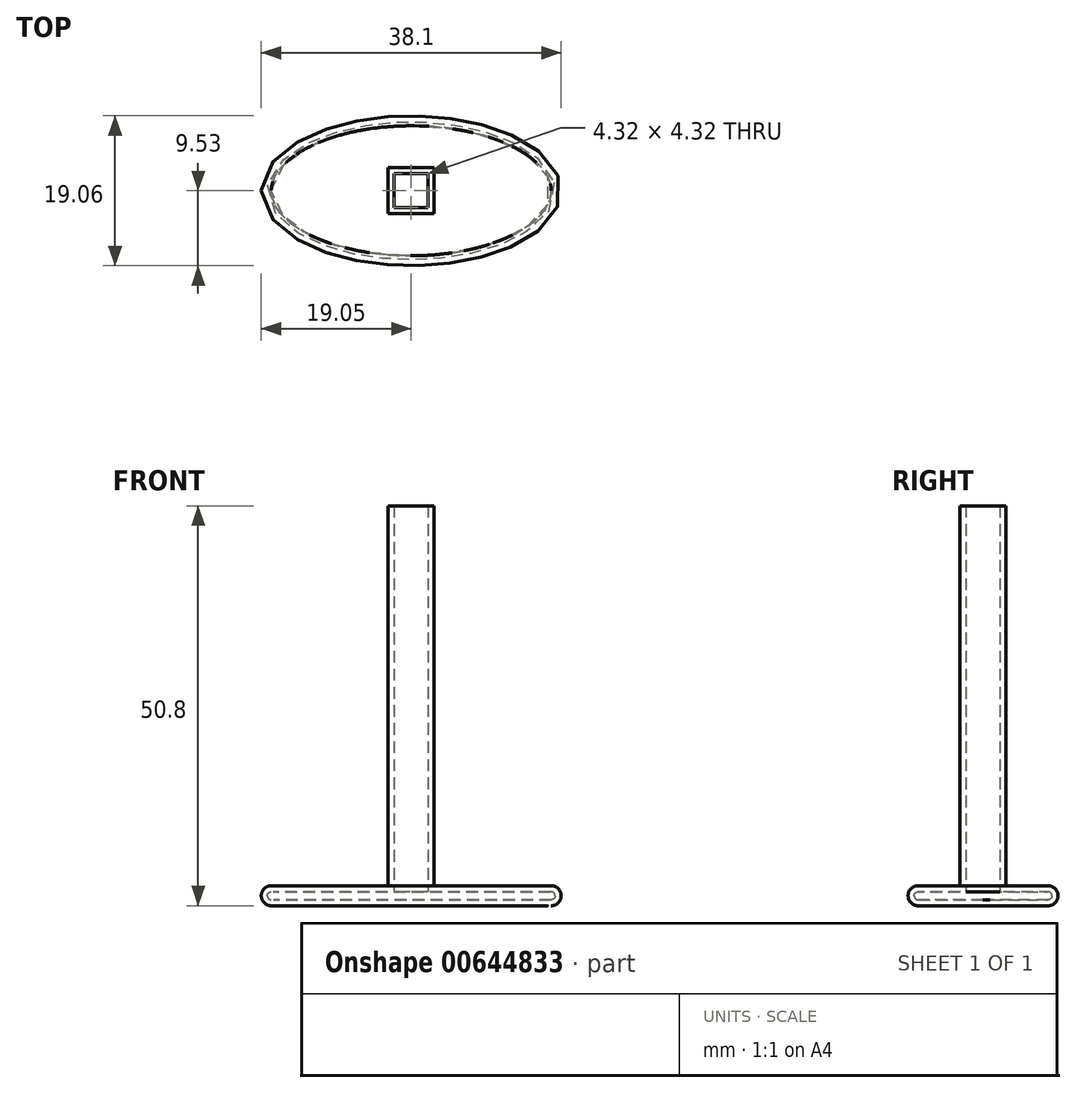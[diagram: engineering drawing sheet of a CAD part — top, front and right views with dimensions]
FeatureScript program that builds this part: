
annotation { "Feature Type Name" : "Feature", "Feature Type Description" : "" }
export const myFeature = defineFeature(function(context is Context, id is Id, definition is map)
    precondition{}
    {
        {
            var Q0;
            Q0=qCreatedBy(makeId("Top.planeOp"),FACE);
            var sketch = newSketch(context, id + "F0", { "sketchPlane" : qUnion([Q0])});
            skLineSegment(sketch, "E0.bottom", {"start": v(2.92, 2.92) * mm, "end": v(-2.92, 2.92) * mm});
            skLineSegment(sketch, "E0.top", {"start": v(2.92, -2.92) * mm, "end": v(-2.92, -2.92) * mm});
            skLineSegment(sketch, "E0.left", {"start": v(2.92, 2.92) * mm, "end": v(2.92, -2.92) * mm});
            skLineSegment(sketch, "E0.right", {"start": v(-2.92, 2.92) * mm, "end": v(-2.92, -2.92) * mm});
            skPoint(sketch, "E0.middle", {"position": v(0, 0) * mm});
            skEllipse(sketch, "E1", {"center": v(0, 0) * mm, "majorRadius": 19.05 * mm, "minorRadius": 9.53 * mm, "majorAxis": v(-1, 0)});
            skSolve(sketch);
        }
        {
            var Q0;
            Q0=makeQuery(id+"F0.imprint","IMPRINT",FACE,{"disambiguationData":[TD([[makeQuery(id+"F0.imprint","IMPRINT",EDGE,{"derivedFrom":sQuery(id+"F0.wireOp",EDGE,"E0.bottom")}),1.0]])]});
            extrude(context, id + "F1", {"entities" : qUnion([Q0]), "depth" : 50.8 * mm, "offsetDistance" : 25.4 * mm});
        }
        {
            var Q0;
            Q0=makeQuery(id+"F0.imprint","IMPRINT",FACE,{"disambiguationData":[TD([[makeQuery(id+"F0.imprint","IMPRINT",EDGE,{"derivedFrom":sQuery(id+"F0.wireOp",EDGE,"E0.bottom")}),-1.0]])]});
            extrude(context, id + "F2", {"entities" : qUnion([Q0]), "operationType" : NewBodyOperationType.ADD, "depth" : 2.54 * mm, "offsetDistance" : 25.4 * mm});
        }
        {
            var Q0;
            Q0=makeQuery(id+"F2.opExtrude","CAP_EDGE",EDGE,{"disambiguationData":[OSD([sQuery(id+"F0.wireOp",EDGE,"E1")])],"isStart":false});
            var Q1;
            Q1=makeQuery(id+"F2.opExtrude","CAP_EDGE",EDGE,{"disambiguationData":[OSD([sQuery(id+"F0.wireOp",EDGE,"E1")])],"isStart":true});
            fillet(context, id + "F3", {"entities" : qUnion([Q0, Q1]), "radius" : 1.27 * mm, "tangentPropagation" : true, "allowEdgeOverflow" : false});
        }
        {
            var Q0;
            Q0=makeQuery(id+"F1.opExtrude","CAP_FACE",FACE,{"disambiguationData":[OSD([sQuery(id+"F0.wireOp",EDGE,"E0.bottom"),sQuery(id+"F0.wireOp",EDGE,"E0.top"),sQuery(id+"F0.wireOp",EDGE,"E0.left"),sQuery(id+"F0.wireOp",EDGE,"E0.right")])],"isStart":false});
            shell(context, id + "F4", {"entities" : qUnion([Q0]), "thickness" : 0.76 * mm});
        }
        {
            var Q0;
            Q0=makeQuery(id+"F0.imprint","IMPRINT",FACE,{"disambiguationData":[TD([[makeQuery(id+"F0.imprint","IMPRINT",EDGE,{"derivedFrom":sQuery(id+"F0.wireOp",EDGE,"E0.bottom")}),-1.0]])]});
            var sketch = newSketch(context, id + "F5", { "sketchPlane" : qUnion([Q0])});
            skCircle(sketch, "E2", {"center": v(-13.19, 0) * mm, "radius": 1.9 * mm});
            skSolve(sketch);
        }
        {
            var Q0;
            Q0=sQuery(id+"F5.wireOp",EDGE,"E2");
            extrude(context, id + "F6", {"bodyType" : ToolBodyType.SURFACE, "surfaceEntities" : qUnion([Q0]), "oppositeDirection" : true, "depth" : 17.78 * mm, "offsetDistance" : 25.4 * mm});
        }
    });
